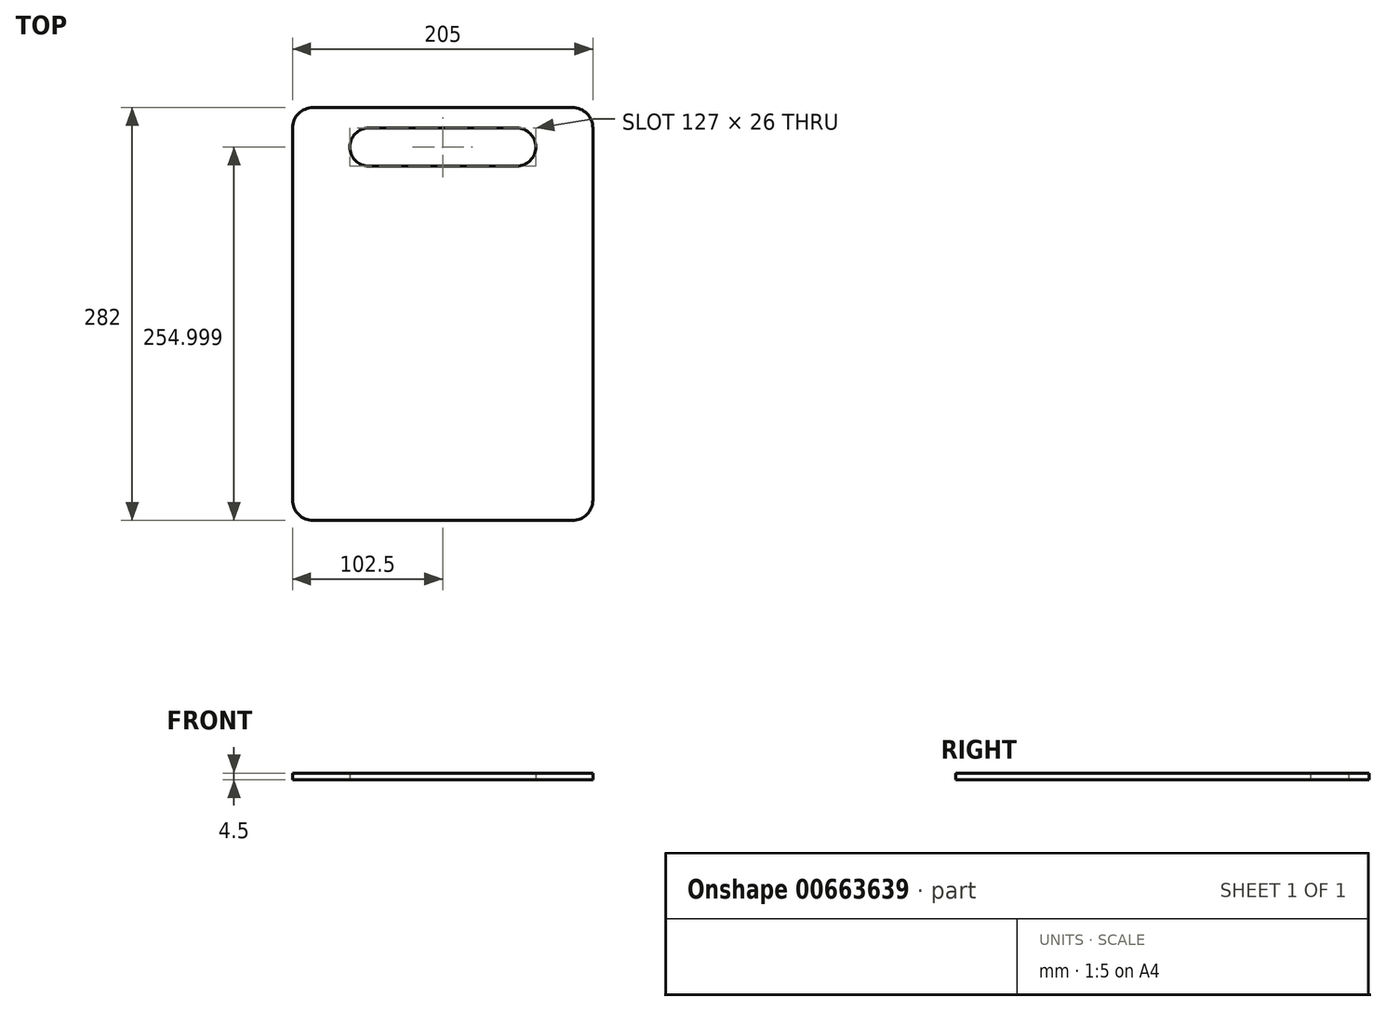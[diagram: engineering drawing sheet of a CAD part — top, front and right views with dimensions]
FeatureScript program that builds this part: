
annotation { "Feature Type Name" : "Feature", "Feature Type Description" : "" }
export const myFeature = defineFeature(function(context is Context, id is Id, definition is map)
    precondition{}
    {
        {
            var Q0;
            Q0=qCreatedBy(makeId("Top.planeOp"),FACE);
            var sketch = newSketch(context, id + "F0", { "sketchPlane" : qUnion([Q0])});
            skLineSegment(sketch, "E0.bottom", {"start": v(-90.62, 144.3) * mm, "end": v(86.38, 144.3) * mm});
            skLineSegment(sketch, "E0.top", {"start": v(-90.62, -137.7) * mm, "end": v(86.38, -137.7) * mm});
            skLineSegment(sketch, "E0.left", {"start": v(-104.62, 130.3) * mm, "end": v(-104.62, -123.7) * mm});
            skLineSegment(sketch, "E0.right", {"start": v(100.38, 130.3) * mm, "end": v(100.38, -123.7) * mm});
            skPoint(sketch, "E1.visualSharp", {"position": v(-104.62, 144.3) * mm});
            skArc(sketch, "E1.filletArc", {"start": v(-90.62, 144.3) * mm, "mid": v(-100.52, 140.2) * mm, "end": v(-104.62, 130.3) * mm});
            skPoint(sketch, "E2.visualSharp", {"position": v(100.38, 144.3) * mm});
            skArc(sketch, "E2.filletArc", {"start": v(100.38, 130.3) * mm, "mid": v(96.28, 140.2) * mm, "end": v(86.38, 144.3) * mm});
            skPoint(sketch, "E3.visualSharp", {"position": v(100.38, -137.7) * mm});
            skArc(sketch, "E3.filletArc", {"start": v(86.38, -137.7) * mm, "mid": v(96.28, -133.6) * mm, "end": v(100.38, -123.7) * mm});
            skPoint(sketch, "E4.visualSharp", {"position": v(-104.62, -137.7) * mm});
            skArc(sketch, "E4.filletArc", {"start": v(-104.62, -123.7) * mm, "mid": v(-100.52, -133.6) * mm, "end": v(-90.62, -137.7) * mm});
            skLineSegment(sketch, "E5.bottom", {"start": v(-52.62, 130.3) * mm, "end": v(48.38, 130.3) * mm});
            skLineSegment(sketch, "E5.top", {"start": v(-52.62, 104.3) * mm, "end": v(48.38, 104.3) * mm});
            skLineSegment(sketch, "E5.left", {"start": v(-65.62, 117.3) * mm, "end": v(-65.62, 117.3) * mm});
            skLineSegment(sketch, "E5.right", {"start": v(61.38, 117.3) * mm, "end": v(61.38, 117.3) * mm});
            skPoint(sketch, "E6", {"position": v(0, 144.3) * mm});
            skPoint(sketch, "E7", {"position": v(-2.12, 104.3) * mm});
            skPoint(sketch, "E8.visualSharp", {"position": v(-65.62, 130.3) * mm});
            skArc(sketch, "E8.filletArc", {"start": v(-52.62, 130.3) * mm, "mid": v(-61.81, 126.5) * mm, "end": v(-65.62, 117.3) * mm});
            skPoint(sketch, "E9.visualSharp", {"position": v(-65.62, 104.3) * mm});
            skArc(sketch, "E9.filletArc", {"start": v(-65.62, 117.3) * mm, "mid": v(-61.81, 108.12) * mm, "end": v(-52.62, 104.3) * mm});
            skPoint(sketch, "E10.visualSharp", {"position": v(61.38, 104.3) * mm});
            skArc(sketch, "E10.filletArc", {"start": v(48.38, 104.3) * mm, "mid": v(57.57, 108.12) * mm, "end": v(61.38, 117.3) * mm});
            skPoint(sketch, "E11.visualSharp", {"position": v(61.38, 130.3) * mm});
            skArc(sketch, "E11.filletArc", {"start": v(61.38, 117.3) * mm, "mid": v(57.57, 126.5) * mm, "end": v(48.38, 130.3) * mm});
            skSolve(sketch);
        }
        {
            var Q0;
            Q0=qSketchRegion(id+"F0",true);
            extrude(context, id + "F1", {"entities" : qUnion([Q0]), "depth" : 4.5 * mm, "offsetDistance" : 25 * mm});
        }
    });
